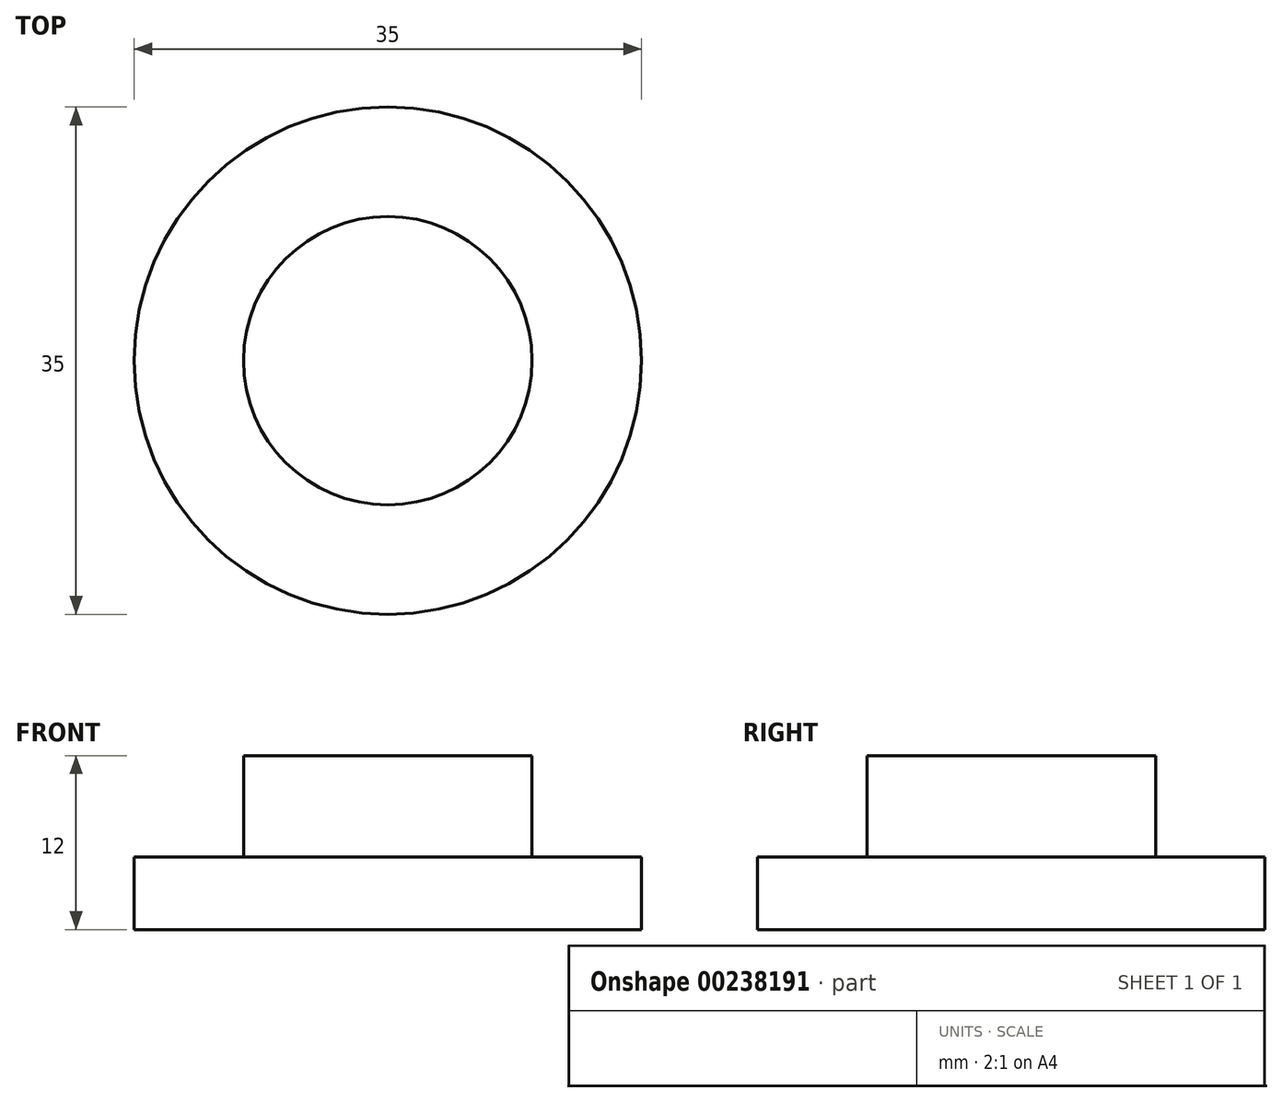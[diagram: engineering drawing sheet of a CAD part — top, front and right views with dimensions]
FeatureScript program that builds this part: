
annotation { "Feature Type Name" : "Feature", "Feature Type Description" : "" }
export const myFeature = defineFeature(function(context is Context, id is Id, definition is map)
    precondition{}
    {
        {
            var Q0;
            Q0=qCreatedBy(makeId("Top.planeOp"),FACE);
            var sketch = newSketch(context, id + "F0", { "sketchPlane" : qUnion([Q0])});
            skCircle(sketch, "E0", {"center": v(0, 0) * mm, "radius": 17.5 * mm});
            skSolve(sketch);
        }
        {
            var Q0;
            Q0 = qSketchRegion(id + "F0", true);
            extrude(context, id + "F1", {"entities" : qUnion([Q0]), "depth" : 5 * mm, "offsetDistance" : 25 * mm});
        }
        {
            var Q0;
            Q0=makeQuery(id+"F1.opExtrude","CAP_FACE",FACE,{"disambiguationData":[OSD([sQuery(id+"F0.wireOp",EDGE,"E0")])],"isStart":false});
            var sketch = newSketch(context, id + "F2", { "sketchPlane" : qUnion([Q0])});
            skCircle(sketch, "E1", {"center": v(0, 0) * mm, "radius": 9.95 * mm});
            skSolve(sketch);
        }
        {
            var Q0;
            Q0 = qSketchRegion(id + "F2", true);
            extrude(context, id + "F3", {"entities" : qUnion([Q0]), "operationType" : NewBodyOperationType.ADD, "depth" : 7 * mm, "offsetDistance" : 25 * mm});
        }
    });
